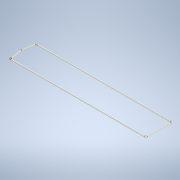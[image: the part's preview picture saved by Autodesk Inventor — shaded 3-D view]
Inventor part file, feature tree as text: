
AUTODESK INVENTOR PART (.ipt)
format: ipt  version: 2021 (Build 250183000, 183)  size: 139,776 bytes
history: native  units: in
note: dims shown in document units (in); Inventor stores cm internally (conversion verified against a paired STEP export)
features: plane x1, sweep x1, sketch x1
ambient origin geometry x8: Origin, YZ Plane, XZ Plane, XY Plane, X Axis, Y Axis, Z Axis, Center Point
bodies: Solid1 (feature_tree)
feature tree (3):
  plane  "Work Plane2"
  sweep  "Sweep1"
  sketch  "Sketch3"  dims[d23=0.25in d24=0.0in d25=0.0in d26=30.0in d27=5.75in d28=0.0in d29=0.0in d30=0.0in d31=0.0in d32=30.0in d34=0.5497in d35=0.125in d36=0.25in]
